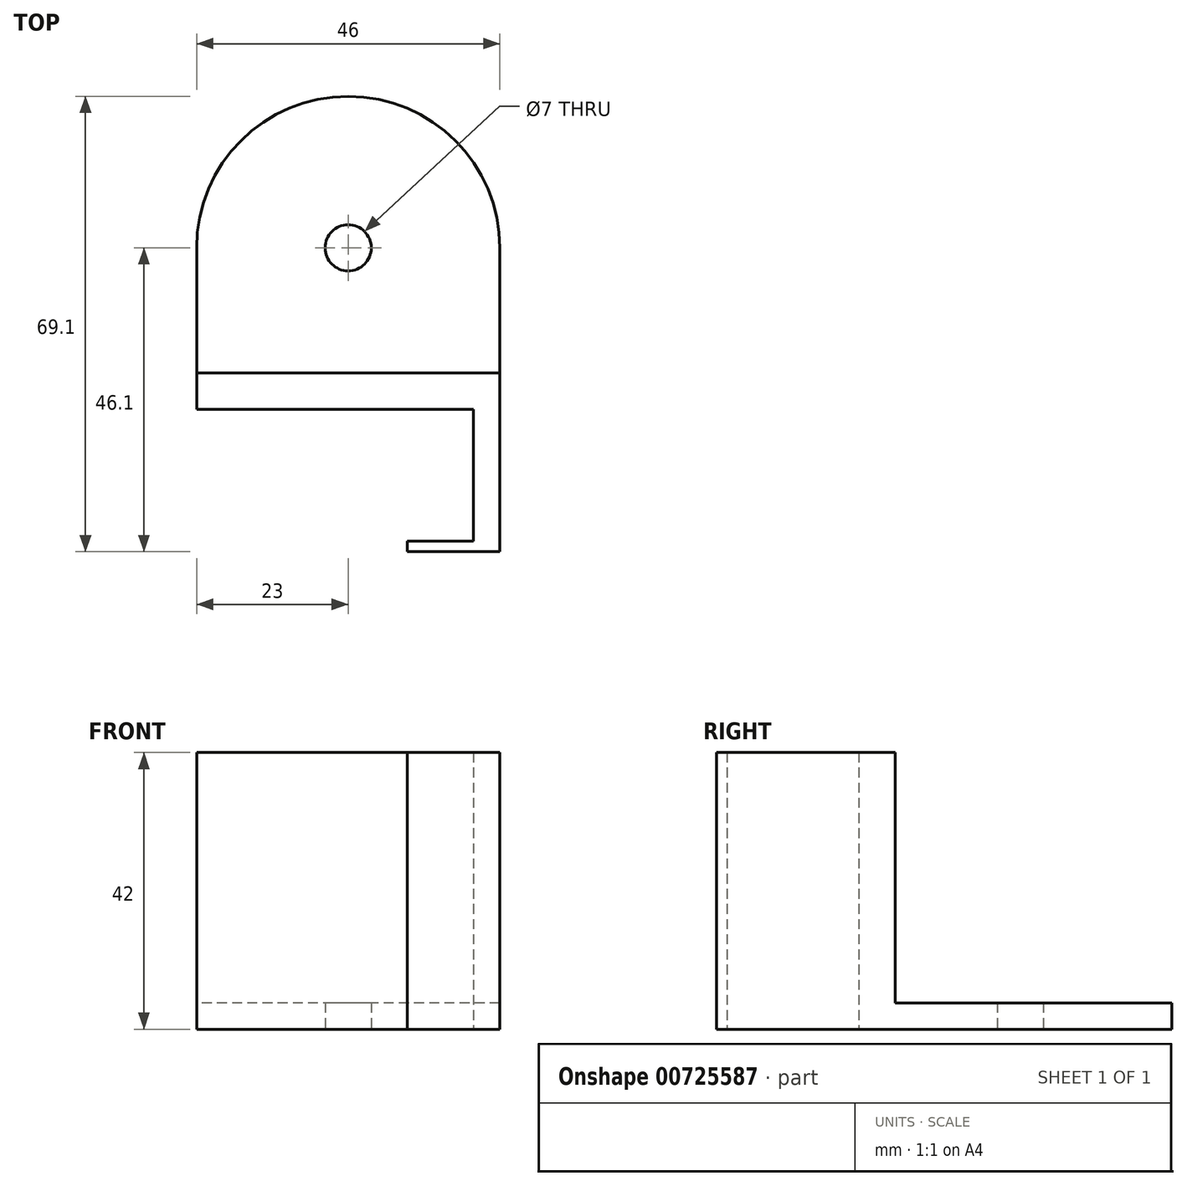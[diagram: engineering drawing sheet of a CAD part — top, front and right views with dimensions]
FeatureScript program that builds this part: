
annotation { "Feature Type Name" : "Feature", "Feature Type Description" : "" }
export const myFeature = defineFeature(function(context is Context, id is Id, definition is map)
    precondition{}
    {
        {
            var Q0;
            Q0=qCreatedBy(makeId("Top.planeOp"),FACE);
            var sketch = newSketch(context, id + "F0", { "sketchPlane" : qUnion([Q0])});
            skArc(sketch, "E0", {"start": v(46, 24.5) * mm, "mid": v(23, 47.5) * mm, "end": v(0, 24.5) * mm});
            skLineSegment(sketch, "E1.top", {"start": v(0, 0) * mm, "end": v(42, 0) * mm});
            skLineSegment(sketch, "E1.left", {"start": v(0, 24.5) * mm, "end": v(0, 0) * mm});
            skLineSegment(sketch, "E1.right", {"start": v(46, 24.5) * mm, "end": v(46, 0) * mm});
            skLineSegment(sketch, "E2", {"start": v(11.82, 47.5) * mm, "end": v(42.8, 47.5) * mm, "construction": true});
            skLineSegment(sketch, "E3.top", {"start": v(42, -21.6) * mm, "end": v(46, -21.6) * mm});
            skLineSegment(sketch, "E3.left", {"start": v(42, 0) * mm, "end": v(42, -20) * mm});
            skLineSegment(sketch, "E3.right", {"start": v(46, 0) * mm, "end": v(46, -21.6) * mm});
            skLineSegment(sketch, "E4.bottom", {"start": v(32, -20) * mm, "end": v(42, -20) * mm});
            skLineSegment(sketch, "E4.top", {"start": v(32, -21.6) * mm, "end": v(46, -21.6) * mm});
            skLineSegment(sketch, "E4.left", {"start": v(32, -20) * mm, "end": v(32, -21.6) * mm});
            skLineSegment(sketch, "E4.right", {"start": v(46, -20) * mm, "end": v(46, -21.6) * mm});
            skArc(sketch, "E5", {"start": v(42, 24.5) * mm, "mid": v(23, 43.5) * mm, "end": v(4, 24.5) * mm});
            skLineSegment(sketch, "E6", {"start": v(23, 52.8) * mm, "end": v(23, -23.62) * mm, "construction": true});
            skPoint(sketch, "E7.middle", {"position": v(64.93, 27.09) * mm});
            skLineSegment(sketch, "E8", {"start": v(56.38, 24.5) * mm, "end": v(-2.56, 24.5) * mm, "construction": true});
            skCircle(sketch, "E9", {"center": v(23, 24.5) * mm, "radius": 3.5 * mm});
            skLineSegment(sketch, "E10", {"start": v(42, 5.5) * mm, "end": v(42, 24.5) * mm});
            skLineSegment(sketch, "E11", {"start": v(0, 5.5) * mm, "end": v(42, 5.5) * mm});
            skLineSegment(sketch, "E12", {"start": v(42, 5.5) * mm, "end": v(46, 5.5) * mm});
            skPoint(sketch, "E13", {"position": v(46, 24.5) * mm});
            skSolve(sketch);
        }
        {
            var Q0;
            Q0=qCreatedBy(makeId("Right.planeOp"),FACE);
            var sketch = newSketch(context, id + "F1", { "sketchPlane" : qUnion([Q0])});
            skLineSegment(sketch, "E14", {"start": v(47.5, 0) * mm, "end": v(47.5, 42) * mm});
            skLineSegment(sketch, "E15", {"start": v(47.5, 42) * mm, "end": v(-21.6, 42) * mm});
            skLineSegment(sketch, "E16", {"start": v(-21.6, 42) * mm, "end": v(-21.6, 0) * mm});
            skLineSegment(sketch, "E17", {"start": v(47.5, 0) * mm, "end": v(-21.6, 0) * mm});
            skLineSegment(sketch, "E18", {"start": v(47.5, 4) * mm, "end": v(-21.6, 4) * mm});
            skSolve(sketch);
        }
        {
            var Q0;
            Q0=makeQuery(id+"F0.imprint","IMPRINT",FACE,{"disambiguationData":[TD([[makeQuery(id+"F0.imprint","IMPRINT",EDGE,{"derivedFrom":sQuery(id+"F0.wireOp",EDGE,"E5")}),1.0]])]});
            var Q1;
            {var subQ1=sQuery(id+"F0.wireOp",EDGE,"E0");Q1=makeQuery(id+"F0.imprint","IMPRINT",FACE,{"disambiguationData":[TD([[makeQuery(id+"F0.imprint","IMPRINT",EDGE,{"derivedFrom":subQ1}),1.0]])]});}
            var Q2;
            {var subQ1=sQuery(id+"F0.wireOp",EDGE,"E3.left");Q2=makeQuery(id+"F0.imprint","IMPRINT",FACE,{"disambiguationData":[TD([[makeQuery(id+"F0.imprint","IMPRINT",EDGE,{"derivedFrom":subQ1}),1.0]])]});}
            var Q3;
            Q3=sQuery(id+"F1.wireOp",VERTEX,"E18.end");
            extrude(context, id + "F2", {"entities" : qUnion([Q0, Q1, Q2]), "endBound" : BoundingType.UP_TO_VERTEX, "depth" : 25 * mm, "endBoundEntityVertex" : qUnion([Q3]), "offsetDistance" : 25 * mm});
        }
        {
            var Q0;
            {var subQ1=sQuery(id+"F0.wireOp",EDGE,"E3.left");Q0=makeQuery(id+"F0.imprint","IMPRINT",FACE,{"disambiguationData":[TD([[makeQuery(id+"F0.imprint","IMPRINT",EDGE,{"derivedFrom":subQ1}),1.0]])]});}
            var Q1;
            {var subQ5=sQuery(id+"F0.wireOp",EDGE,"E11");Q1=makeQuery(id+"F0.imprint","IMPRINT",FACE,{"disambiguationData":[TD([[makeQuery(id+"F0.imprint","IMPRINT",EDGE,{"derivedFrom":subQ5}),-1.0]])]});}
            var Q2;
            Q2=sQuery(id+"F1.wireOp",VERTEX,"E15.end");
            extrude(context, id + "F3", {"entities" : qUnion([Q0, Q1]), "operationType" : NewBodyOperationType.ADD, "endBound" : BoundingType.UP_TO_VERTEX, "depth" : 25 * mm, "endBoundEntityVertex" : qUnion([Q2]), "offsetDistance" : 25 * mm});
        }
    });
